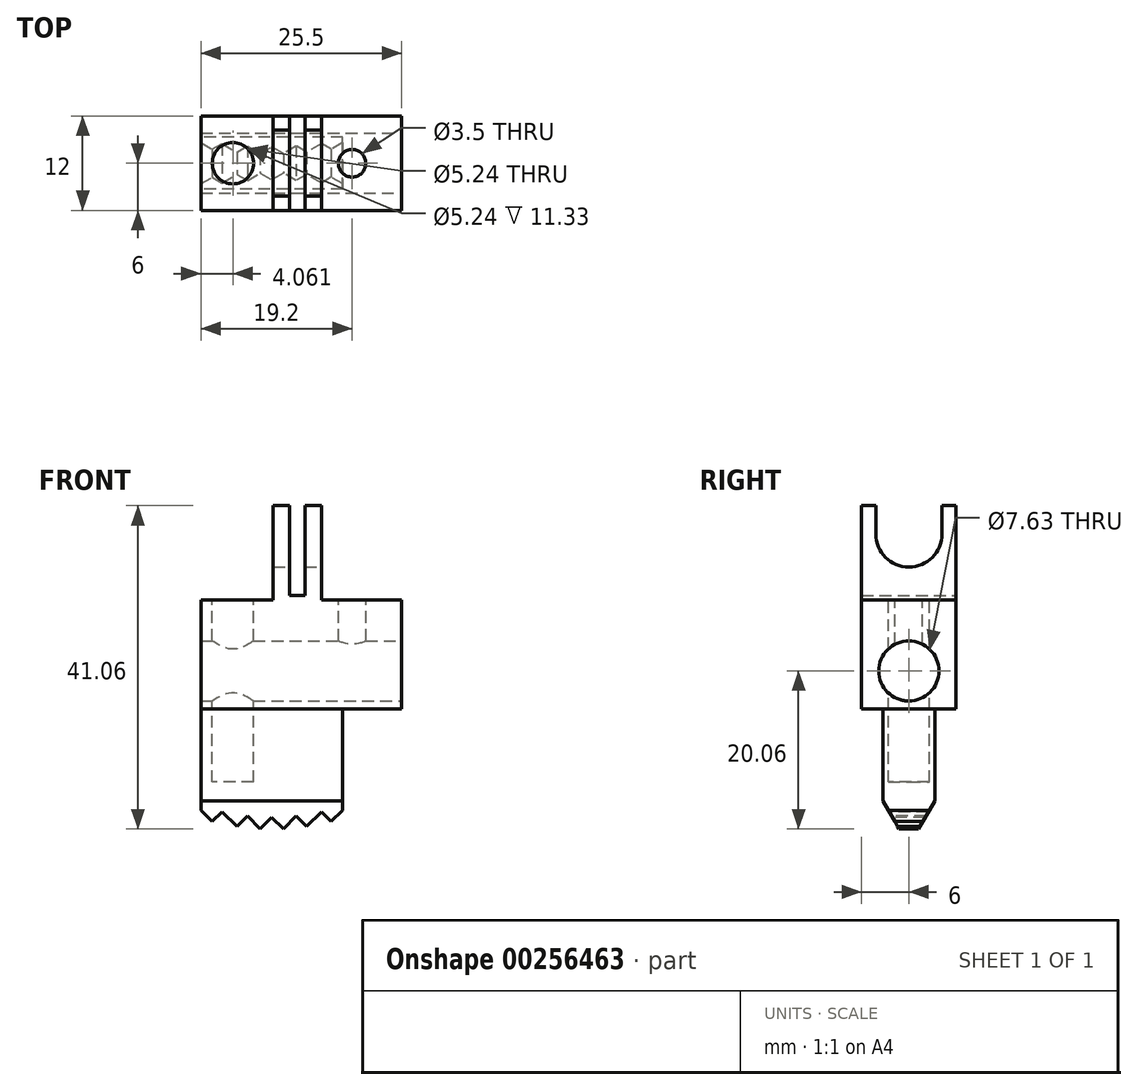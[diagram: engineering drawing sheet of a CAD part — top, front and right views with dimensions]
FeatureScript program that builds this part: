
annotation { "Feature Type Name" : "Feature", "Feature Type Description" : "" }
export const myFeature = defineFeature(function(context is Context, id is Id, definition is map)
    precondition{}
    {
        {
            var Q0;
            Q0=qCreatedBy(makeId("Front.planeOp"),FACE);
            var sketch = newSketch(context, id + "F0", { "sketchPlane" : qUnion([Q0])});
            skLineSegment(sketch, "E0", {"start": v(0, 0) * mm, "end": v(-6, 0) * mm});
            skLineSegment(sketch, "E1", {"start": v(0, 0) * mm, "end": v(0, 5.1) * mm});
            skLineSegment(sketch, "E2", {"start": v(0, 5.1) * mm, "end": v(2.5, 5.1) * mm});
            skLineSegment(sketch, "E3", {"start": v(2.5, 5.1) * mm, "end": v(2.5, 9.7) * mm});
            skLineSegment(sketch, "E4", {"start": v(2.5, 9.7) * mm, "end": v(-0.9, 9.7) * mm});
            skLineSegment(sketch, "E5", {"start": v(-0.9, 9.7) * mm, "end": v(-0.9, 13.7) * mm});
            skLineSegment(sketch, "E6", {"start": v(-0.9, 13.7) * mm, "end": v(-1.6, 13.7) * mm});
            skLineSegment(sketch, "E7", {"start": v(-1.6, 13.7) * mm, "end": v(-1.6, 9.9) * mm});
            skLineSegment(sketch, "E8", {"start": v(-1.6, 9.9) * mm, "end": v(-2.25, 9.9) * mm});
            skLineSegment(sketch, "E9", {"start": v(-2.25, 9.9) * mm, "end": v(-2.25, 13.7) * mm});
            skLineSegment(sketch, "E10", {"start": v(-2.25, 13.7) * mm, "end": v(-2.95, 13.7) * mm});
            skLineSegment(sketch, "E11", {"start": v(-2.95, 13.7) * mm, "end": v(-2.95, 9.7) * mm});
            skLineSegment(sketch, "E12", {"start": v(-2.95, 9.7) * mm, "end": v(-6, 9.7) * mm});
            skLineSegment(sketch, "E13", {"start": v(-6, 9.7) * mm, "end": v(-6, 0) * mm});
            skLineSegment(sketch, "E14", {"start": v(-3, 0) * mm, "end": v(-3, 10) * mm, "construction": true});
            skCircle(sketch, "E15", {"center": v(-3, 10) * mm, "radius": 10 * mm, "construction": true});
            skLineSegment(sketch, "E16", {"start": v(0, 5.1) * mm, "end": v(-6, 5.1) * mm});
            skSolve(sketch);
        }
        {
            var Q0;
            Q0=makeQuery(id+"F0.imprint","IMPRINT",FACE,{"disambiguationData":[TD([[makeQuery(id+"F0.imprint","IMPRINT",EDGE,{"derivedFrom":sQuery(id+"F0.wireOp",EDGE,"E2")}),1.0]])]});
            extrude(context, id + "F1", {"entities" : qUnion([Q0]), "depth" : 4 * mm, "symmetric" : true});
        }
        {
            var Q0;
            {var subQ2=sQuery(id+"F0.wireOp",EDGE,"E0");Q0=makeQuery(id+"F0.imprint","IMPRINT",FACE,{"disambiguationData":[TD([[makeQuery(id+"F0.imprint","IMPRINT",EDGE,{"derivedFrom":subQ2}),-1.0]])]});}
            extrude(context, id + "F2", {"entities" : qUnion([Q0]), "operationType" : NewBodyOperationType.ADD, "depth" : 2.2 * mm, "symmetric" : true});
        }
        {
            var Q0;
            Q0=makeQuery(id+"F1.opExtrude","SWEPT_FACE",FACE,{"disambiguationData":[OSD([sQuery(id+"F0.wireOp",EDGE,"E5")])]});
            var sketch = newSketch(context, id + "F3", { "sketchPlane" : qUnion([Q0])});
            skLineSegment(sketch, "E17", {"start": v(2, 11.1) * mm, "end": v(-2, 11.1) * mm, "construction": true});
            skArc(sketch, "E18", {"start": v(-1.4, 12.5) * mm, "mid": v(0, 11.1) * mm, "end": v(1.4, 12.5) * mm});
            skLineSegment(sketch, "E19", {"start": v(-1.4, 12.5) * mm, "end": v(-1.4, 13.9) * mm});
            skLineSegment(sketch, "E20", {"start": v(-1.4, 13.9) * mm, "end": v(1.4, 13.9) * mm});
            skLineSegment(sketch, "E21", {"start": v(1.4, 13.9) * mm, "end": v(1.4, 12.5) * mm});
            skSolve(sketch);
        }
        {
            var Q0;
            {var subQ5=sQuery(id+"F3.wireOp",EDGE,"E20");Q0=makeQuery(id+"F3.imprint","IMPRINT",FACE,{"disambiguationData":[TD([[makeQuery(id+"F3.imprint","IMPRINT",EDGE,{"derivedFrom":subQ5}),-1.0]])]});}
            var Q1;
            {var subQ5=sQuery(id+"F3.wireOp",EDGE,"E18");Q1=makeQuery(id+"F3.imprint","IMPRINT",FACE,{"disambiguationData":[TD([[makeQuery(id+"F3.imprint","IMPRINT",EDGE,{"derivedFrom":subQ5}),1.0]])]});}
            var Q2;
            Q2=makeQuery(id+"F1.opExtrude","SWEPT_FACE",FACE,{"disambiguationData":[OSD([sQuery(id+"F0.wireOp",EDGE,"E11")])]});
            extrude(context, id + "F4", {"entities" : qUnion([Q0, Q1]), "operationType" : NewBodyOperationType.REMOVE, "endBound" : BoundingType.UP_TO_SURFACE, "oppositeDirection" : true, "endBoundEntityFace" : qUnion([Q2]), "depth" : 2 * mm});
        }
        {
            var Q0;
            Q0=makeQuery(id+"F1.opExtrude","SWEPT_FACE",FACE,{"disambiguationData":[OSD([sQuery(id+"F0.wireOp",EDGE,"E3")])]});
            var sketch = newSketch(context, id + "F5", { "sketchPlane" : qUnion([Q0])});
            skLineSegment(sketch, "E22", {"start": v(0, 9.7) * mm, "end": v(0, 6.7) * mm, "construction": true});
            skCircle(sketch, "E23", {"center": v(0, 6.7) * mm, "radius": 1.27 * mm});
            skSolve(sketch);
        }
        {
            var Q0;
            Q0=makeQuery(id+"F5.imprint","IMPRINT",FACE,{"disambiguationData":[TD([[makeQuery(id+"F5.imprint","IMPRINT",EDGE,{"derivedFrom":sQuery(id+"F5.wireOp",EDGE,"E23")}),1.0]])]});
            extrude(context, id + "F6", {"entities" : qUnion([Q0]), "operationType" : NewBodyOperationType.REMOVE, "oppositeDirection" : true, "depth" : 8.5 * mm});
        }
        {
            var Q0;
            Q0=makeQuery(id+"F1.opExtrude","SWEPT_FACE",FACE,{"disambiguationData":[OSD([sQuery(id+"F0.wireOp",EDGE,"E4")])]});
            var sketch = newSketch(context, id + "F7", { "sketchPlane" : qUnion([Q0])});
            skCircle(sketch, "E24", {"center": v(0.4, 0) * mm, "radius": 0.58 * mm});
            skSolve(sketch);
        }
        {
            var Q0;
            Q0=makeQuery(id+"F7.imprint","IMPRINT",FACE,{"disambiguationData":[TD([[makeQuery(id+"F7.imprint","IMPRINT",EDGE,{"derivedFrom":sQuery(id+"F7.wireOp",EDGE,"E24")}),1.0]])]});
            extrude(context, id + "F8", {"entities" : qUnion([Q0]), "operationType" : NewBodyOperationType.REMOVE, "oppositeDirection" : true, "depth" : 3 * mm});
        }
        {
            var Q0;
            Q0=makeQuery(id+"F1.opExtrude","SWEPT_FACE",FACE,{"disambiguationData":[OSD([sQuery(id+"F0.wireOp",EDGE,"E12")])]});
            var sketch = newSketch(context, id + "F9", { "sketchPlane" : qUnion([Q0])});
            skLineSegment(sketch, "E25", {"start": v(-4.65, 2) * mm, "end": v(-4.65, -2) * mm, "construction": true});
            skCircle(sketch, "E26", {"center": v(-4.65, 0) * mm, "radius": 0.87 * mm});
            skSolve(sketch);
        }
        {
            var Q0;
            Q0=makeQuery(id+"F9.imprint","IMPRINT",FACE,{"disambiguationData":[TD([[makeQuery(id+"F9.imprint","IMPRINT",EDGE,{"derivedFrom":sQuery(id+"F9.wireOp",EDGE,"E26")}),1.0]])]});
            extrude(context, id + "F10", {"entities" : qUnion([Q0]), "operationType" : NewBodyOperationType.REMOVE, "oppositeDirection" : true, "depth" : 7.7 * mm});
        }
        {
            var Q0;
            Q0=makeQuery(id+"F2.opExtrude","CAP_EDGE",EDGE,{"disambiguationData":[OSD([sQuery(id+"F0.wireOp",EDGE,"E0")])],"isStart":false});
            var Q1;
            Q1=makeQuery(id+"F2.opExtrude","CAP_EDGE",EDGE,{"disambiguationData":[OSD([sQuery(id+"F0.wireOp",EDGE,"E0")])],"isStart":true});
            chamfer(context, id + "F11", {"entities" : qUnion([Q0, Q1]), "chamferType" : ChamferType.OFFSET_ANGLE, "width" : 1.2 * mm, "oppositeDirection" : true, "angle" : 30 * degree, "tangentPropagation" : true});
        }
        {
            var Q0;
            Q0=qCreatedBy(makeId("Front.planeOp"),FACE);
            var sketch = newSketch(context, id + "F12", { "sketchPlane" : qUnion([Q0])});
            skCircle(sketch, "E27", {"center": v(-3, 10) * mm, "radius": 10 * mm, "construction": true});
            skPoint(sketch, "E28", {"position": v(-3, 0) * mm});
            skCircle(sketch, "E29", {"center": v(-3, 10) * mm, "radius": 9.5 * mm, "construction": true});
            skLineSegment(sketch, "E30", {"start": v(-3, 0.5) * mm, "end": v(-3.49, 0.01) * mm});
            skLineSegment(sketch, "E31", {"start": v(-3, 0.5) * mm, "end": v(-2.51, 0.01) * mm});
            skLineSegment(sketch, "E32", {"start": v(-3.49, 0.01) * mm, "end": v(-4.03, 0.56) * mm});
            skLineSegment(sketch, "E33", {"start": v(-4.03, 0.56) * mm, "end": v(-4.48, 0.1) * mm});
            skLineSegment(sketch, "E34", {"start": v(-4.48, 0.1) * mm, "end": v(-5.1, 0.74) * mm});
            skLineSegment(sketch, "E35", {"start": v(-5.1, 0.74) * mm, "end": v(-5.52, 0.32) * mm});
            skLineSegment(sketch, "E36", {"start": v(-5.52, 0.32) * mm, "end": v(-6, 0.8) * mm});
            skLineSegment(sketch, "E37", {"start": v(-6, 0.8) * mm, "end": v(-6, 0) * mm});
            skLineSegment(sketch, "E38", {"start": v(-6, 0) * mm, "end": v(0, 0) * mm});
            skLineSegment(sketch, "E39", {"start": v(0, 0) * mm, "end": v(0, 0.8) * mm});
            skLineSegment(sketch, "E40", {"start": v(-2.51, 0.01) * mm, "end": v(-1.97, 0.56) * mm});
            skLineSegment(sketch, "E41", {"start": v(-1.97, 0.56) * mm, "end": v(-1.52, 0.1) * mm});
            skLineSegment(sketch, "E42", {"start": v(-1.52, 0.1) * mm, "end": v(-0.9, 0.74) * mm});
            skLineSegment(sketch, "E43", {"start": v(-0.9, 0.74) * mm, "end": v(-0.48, 0.32) * mm});
            skLineSegment(sketch, "E44", {"start": v(-0.48, 0.32) * mm, "end": v(0, 0.8) * mm});
            skSolve(sketch);
        }
        {
            var Q0;
            Q0=makeQuery(id+"F12.imprint","IMPRINT",FACE,{"disambiguationData":[TD([[makeQuery(id+"F12.imprint","IMPRINT",EDGE,{"derivedFrom":sQuery(id+"F12.wireOp",EDGE,"E30")}),1.0]])]});
            extrude(context, id + "F13", {"entities" : qUnion([Q0]), "operationType" : NewBodyOperationType.REMOVE, "oppositeDirection" : true, "depth" : 25 * mm, "symmetric" : true});
        }
        {
            var Q0;
            Q0=makeQuery(id+"F1.opExtrude","SWEPT_BODY",BODY,{"disambiguationData":[OSD([sQuery(id+"F0.wireOp",EDGE,"E2"),sQuery(id+"F0.wireOp",EDGE,"E3"),sQuery(id+"F0.wireOp",EDGE,"E4"),sQuery(id+"F0.wireOp",EDGE,"E5"),sQuery(id+"F0.wireOp",EDGE,"E6"),sQuery(id+"F0.wireOp",EDGE,"E7"),sQuery(id+"F0.wireOp",EDGE,"E8"),sQuery(id+"F0.wireOp",EDGE,"E9"),sQuery(id+"F0.wireOp",EDGE,"E10"),sQuery(id+"F0.wireOp",EDGE,"E11"),sQuery(id+"F0.wireOp",EDGE,"E12"),sQuery(id+"F0.wireOp",EDGE,"E13"),sQuery(id+"F0.wireOp",EDGE,"E16")])]});
            var Q1;
            Q1=qCreatedBy(makeId("Origin.pointOp"),VERTEX);
            transform(context, id + "F14", {"entities" : qUnion([Q0]), "transformType" : TransformType.SCALE_UNIFORMLY, "scale" : 3, "makeCopy" : false, "scalePoint" : qUnion([Q1])});
        }
    });
